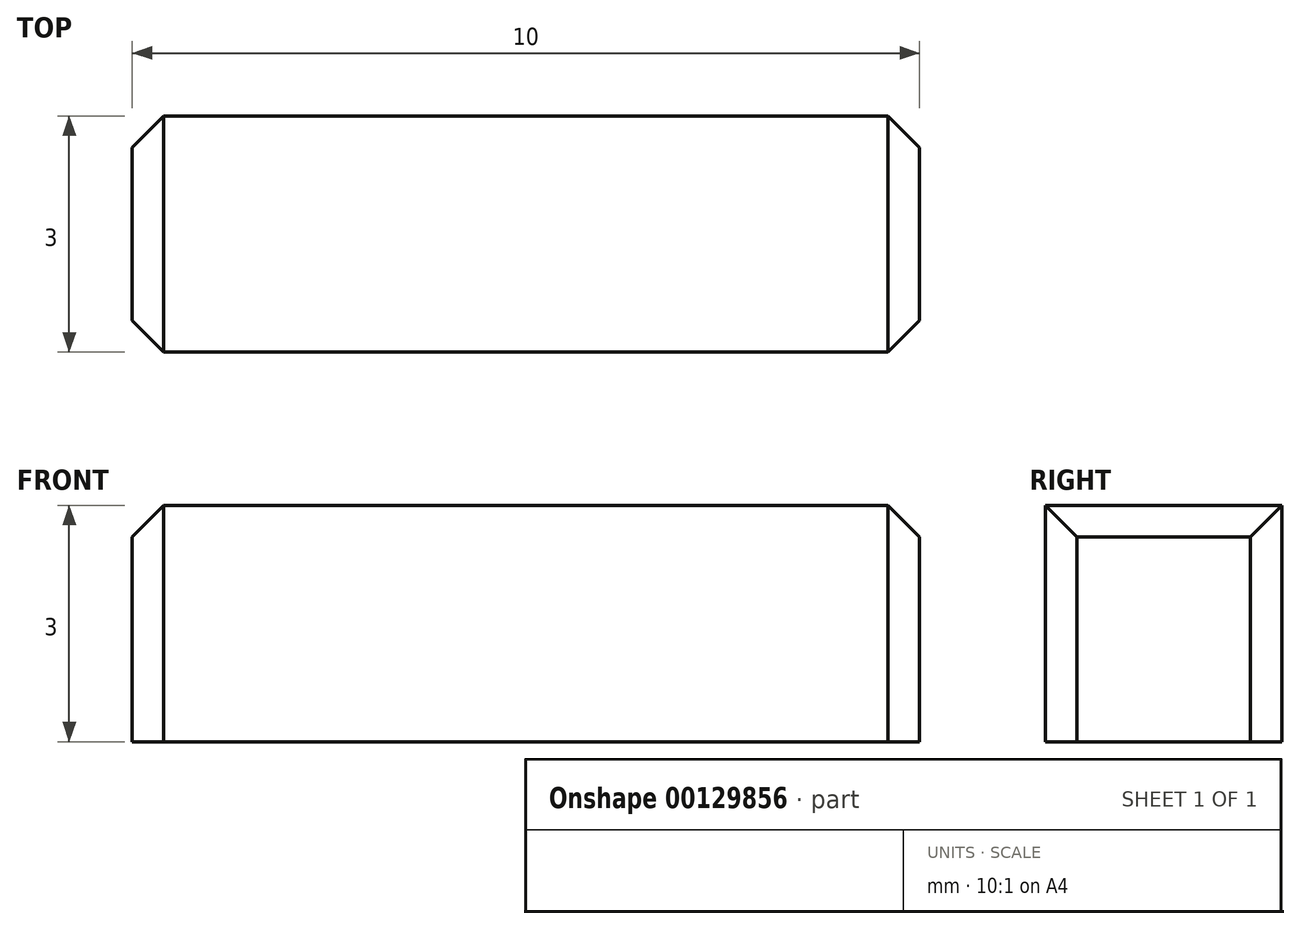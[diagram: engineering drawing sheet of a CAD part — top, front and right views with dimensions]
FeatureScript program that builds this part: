
annotation { "Feature Type Name" : "Feature", "Feature Type Description" : "" }
export const myFeature = defineFeature(function(context is Context, id is Id, definition is map)
    precondition{}
    {
        {
            var Q0;
            Q0=qCreatedBy(makeId("Top.planeOp"),FACE);
            var sketch = newSketch(context, id + "F0", { "sketchPlane" : qUnion([Q0])});
            skLineSegment(sketch, "E0.bottom", {"start": v(5, -1.5) * mm, "end": v(-5, -1.5) * mm});
            skLineSegment(sketch, "E0.top", {"start": v(5, 1.5) * mm, "end": v(-5, 1.5) * mm});
            skLineSegment(sketch, "E0.left", {"start": v(5, -1.5) * mm, "end": v(5, 1.5) * mm});
            skLineSegment(sketch, "E0.right", {"start": v(-5, -1.5) * mm, "end": v(-5, 1.5) * mm});
            skPoint(sketch, "E0.middle", {"position": v(0, 0) * mm});
            skSolve(sketch);
        }
        {
            var Q0;
            Q0 = qSketchRegion(id + "F0", true);
            var Q1;
            Q1=makeQuery(id+"F0.imprint","IMPRINT",FACE,{"disambiguationData":[TD([[makeQuery(id+"F0.imprint","IMPRINT",EDGE,{"derivedFrom":sQuery(id+"F0.wireOp",EDGE,"E0.bottom")}),-1.0]])]});
            extrude(context, id + "F1", {"entities" : qUnion([Q0, Q1]), "depth" : 3 * mm});
        }
        {
            var Q0;
            Q0=makeQuery(id+"F1.opExtrude","CAP_EDGE",EDGE,{"disambiguationData":[OSD([sQuery(id+"F0.wireOp",EDGE,"E0.right")])],"isStart":false});
            var Q1;
            Q1=makeQuery(id+"F1.opExtrude","CAP_EDGE",EDGE,{"disambiguationData":[OSD([sQuery(id+"F0.wireOp",EDGE,"E0.left")])],"isStart":false});
            chamfer(context, id + "F2", {"entities" : qUnion([Q0, Q1]), "width" : 0.4 * mm, "tangentPropagation" : true});
        }
        {
            var Q0;
            Q0=makeQuery(id+"F1.opExtrude","SWEPT_EDGE",EDGE,{"disambiguationData":[OSD([sQuery(id+"F0.wireOp",EDGE,"E0.bottom"),sQuery(id+"F0.wireOp",EDGE,"E0.left")])]});
            var Q1;
            Q1=makeQuery(id+"F1.opExtrude","SWEPT_EDGE",EDGE,{"disambiguationData":[OSD([sQuery(id+"F0.wireOp",EDGE,"E0.top"),sQuery(id+"F0.wireOp",EDGE,"E0.left")])]});
            var Q2;
            Q2=makeQuery(id+"F1.opExtrude","SWEPT_EDGE",EDGE,{"disambiguationData":[OSD([sQuery(id+"F0.wireOp",EDGE,"E0.bottom"),sQuery(id+"F0.wireOp",EDGE,"E0.right")])]});
            var Q3;
            Q3=makeQuery(id+"F1.opExtrude","SWEPT_EDGE",EDGE,{"disambiguationData":[OSD([sQuery(id+"F0.wireOp",EDGE,"E0.top"),sQuery(id+"F0.wireOp",EDGE,"E0.right")])]});
            chamfer(context, id + "F3", {"entities" : qUnion([Q0, Q1, Q2, Q3]), "width" : 0.4 * mm, "tangentPropagation" : true});
        }
    });
